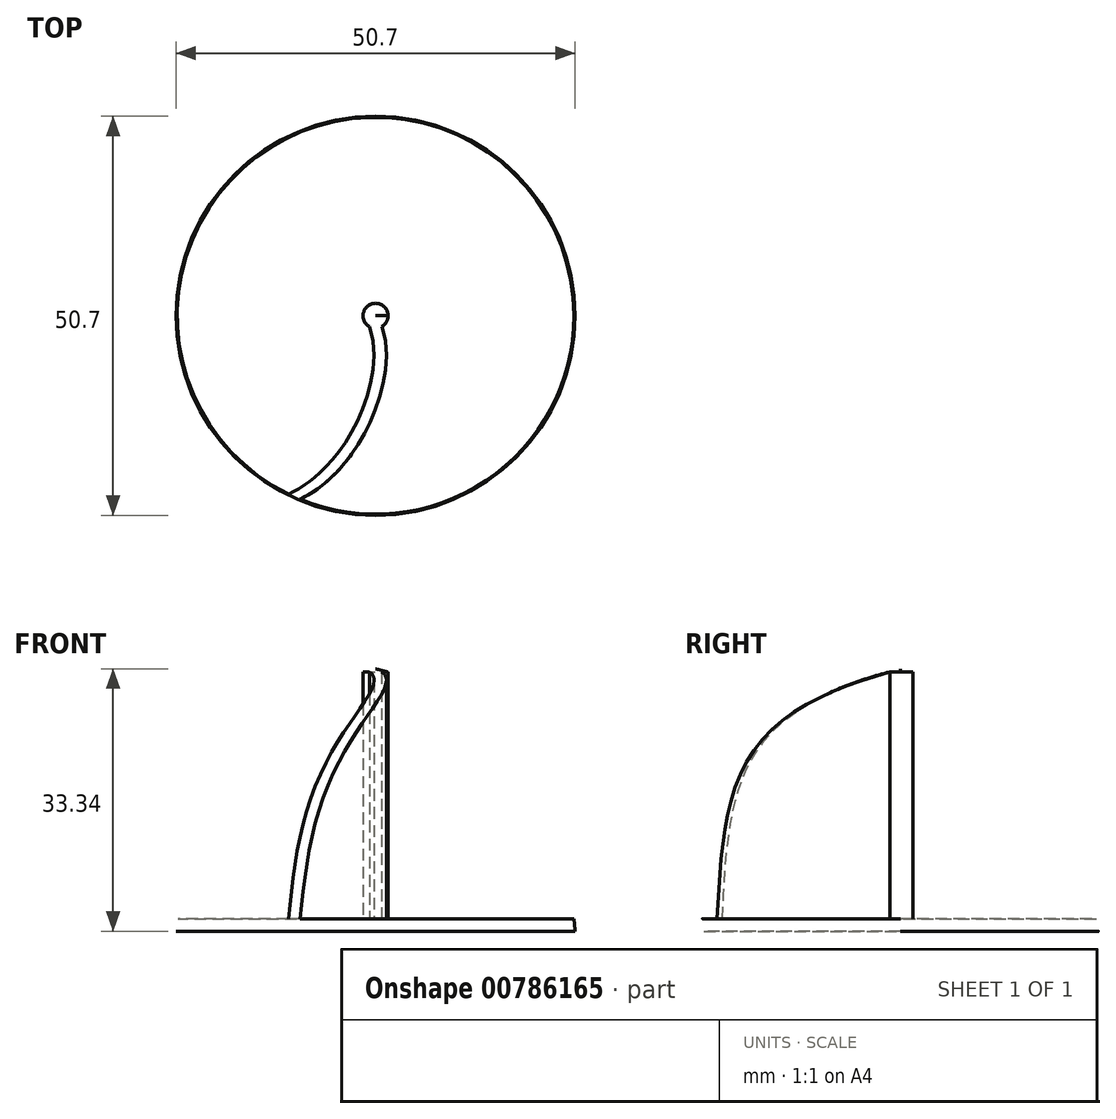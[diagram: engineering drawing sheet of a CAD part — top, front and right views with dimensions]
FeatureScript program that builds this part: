
annotation { "Feature Type Name" : "Feature", "Feature Type Description" : "" }
export const myFeature = defineFeature(function(context is Context, id is Id, definition is map)
    precondition{}
    {
        {
            var Q0;
            Q0=qCreatedBy(makeId("Top.planeOp"),FACE);
            var sketch = newSketch(context, id + "F0", { "sketchPlane" : qUnion([Q0])});
            skCircle(sketch, "E0", {"center": v(0, 0) * mm, "radius": 25.4 * mm});
            skSolve(sketch);
        }
        {
            var Q0;
            Q0 = qSketchRegion(id + "F0", true);
            extrude(context, id + "F1", {"entities" : qUnion([Q0]), "depth" : 1.59 * mm, "offsetDistance" : 25.4 * mm});
        }
        {
            var Q0;
            Q0=makeQuery(id+"F1.opExtrude","CAP_FACE",FACE,{"disambiguationData":[OSD([sQuery(id+"F0.wireOp",EDGE,"E0")])],"isStart":false});
            var sketch = newSketch(context, id + "F2", { "sketchPlane" : qUnion([Q0])});
            skCircle(sketch, "E1", {"center": v(0, 0) * mm, "radius": 1.59 * mm});
            skSolve(sketch);
        }
        {
            var Q0;
            Q0 = qSketchRegion(id + "F2", true);
            extrude(context, id + "F3", {"entities" : qUnion([Q0]), "operationType" : NewBodyOperationType.ADD, "depth" : 31.75 * mm, "offsetDistance" : 25.4 * mm});
        }
        {
            var Q0;
            Q0=makeQuery(id+"F1.opExtrude","CAP_FACE",FACE,{"disambiguationData":[OSD([sQuery(id+"F0.wireOp",EDGE,"E0")])],"isStart":false});
            var sketch = newSketch(context, id + "F4", { "sketchPlane" : qUnion([Q0])});
            skLineSegment(sketch, "E2", {"start": v(0, 30.89) * mm, "end": v(0, -38.93) * mm, "construction": true});
            skLineSegment(sketch, "E3", {"start": v(-0.8, -1.37) * mm, "end": v(0.8, -1.37) * mm});
            skPoint(sketch, "E4", {"position": v(0, -1.37) * mm});
            skFitSpline(sketch, "E5", {"points": [v(-0.8, -1.37) * mm, v(-11.28, -22.76) * mm], "startDerivative": vector(6.92, -16.72) * mm, "endDerivative": vector(-25.34, -11.44) * mm});
            skLineSegment(sketch, "E6", {"start": v(-11.28, -22.76) * mm, "end": v(-9.84, -23.42) * mm});
            skFitSpline(sketch, "E7", {"points": [v(0.8, -1.37) * mm, v(-9.84, -23.42) * mm], "startDerivative": vector(6.92, -16.72) * mm, "endDerivative": vector(-25.34, -11.44) * mm});
            skSolve(sketch);
        }
        {
            var Q0;
            Q0 = qSketchRegion(id + "F4", true);
            var Q1;
            Q1=makeQuery(id+"F3.opExtrude","CAP_FACE",FACE,{"disambiguationData":[OSD([sQuery(id+"F2.wireOp",EDGE,"E1")])],"isStart":false});
            extrude(context, id + "F5", {"entities" : qUnion([Q0]), "operationType" : NewBodyOperationType.ADD, "endBound" : BoundingType.UP_TO_SURFACE, "depth" : 25.4 * mm, "endBoundEntityFace" : qUnion([Q1]), "offsetDistance" : 25.4 * mm});
        }
        {
            var Q0;
            Q0=qCreatedBy(makeId("Front.planeOp"),FACE);
            var sketch = newSketch(context, id + "F6", { "sketchPlane" : qUnion([Q0])});
            skFitSpline(sketch, "E8.1", {"points": [v(0.8, 33.34) * mm, v(5.24, 33.34) * mm, v(9.69, 33.34) * mm, v(14.14, 33.34) * mm], "construction": true});
            skLineSegment(sketch, "E9", {"start": v(0, 0) * mm, "end": v(0, 48.51) * mm, "construction": true});
            skLineSegment(sketch, "E10", {"start": v(0, 0) * mm, "end": v(37.4, 0) * mm, "construction": true});
            skPoint(sketch, "E11", {"position": v(0, 33.34) * mm});
            skLineSegment(sketch, "E12.0", {"start": v(25.35, 33.34) * mm, "end": v(25.35, 1.59) * mm, "construction": true});
            skPoint(sketch, "E13", {"position": v(25.35, 0) * mm});
            skFitSpline(sketch, "E14", {"points": [v(0, 33.34) * mm, v(25.35, 0) * mm], "startDerivative": vector(71.1, -17.72) * mm, "endDerivative": vector(4.06, -44.13) * mm});
            skLineSegment(sketch, "E15", {"start": v(0, 33.34) * mm, "end": v(0, 36.75) * mm});
            skLineSegment(sketch, "E16", {"start": v(0, 36.75) * mm, "end": v(31.98, 36.75) * mm});
            skLineSegment(sketch, "E17", {"start": v(31.98, 36.75) * mm, "end": v(31.98, 0) * mm});
            skLineSegment(sketch, "E18", {"start": v(31.98, 0) * mm, "end": v(25.35, 0) * mm});
            skSolve(sketch);
        }
        {
            var Q0;
            Q0 = qSketchRegion(id + "F6", true);
            var Q1;
            Q1=makeQuery(id+"F1.opExtrude","SWEPT_FACE",FACE,{"disambiguationData":[OSD([sQuery(id+"F0.wireOp",EDGE,"E0")])]});
            revolve(context, id + "F7", {"operationType" : NewBodyOperationType.REMOVE, "surfaceOperationType" : NewSurfaceOperationType.NEW, "entities" : qUnion([Q0]), "axis" : qUnion([Q1]), "revolveType" : RevolveType.FULL, "oppositeDirection" : true});
        }
    });
